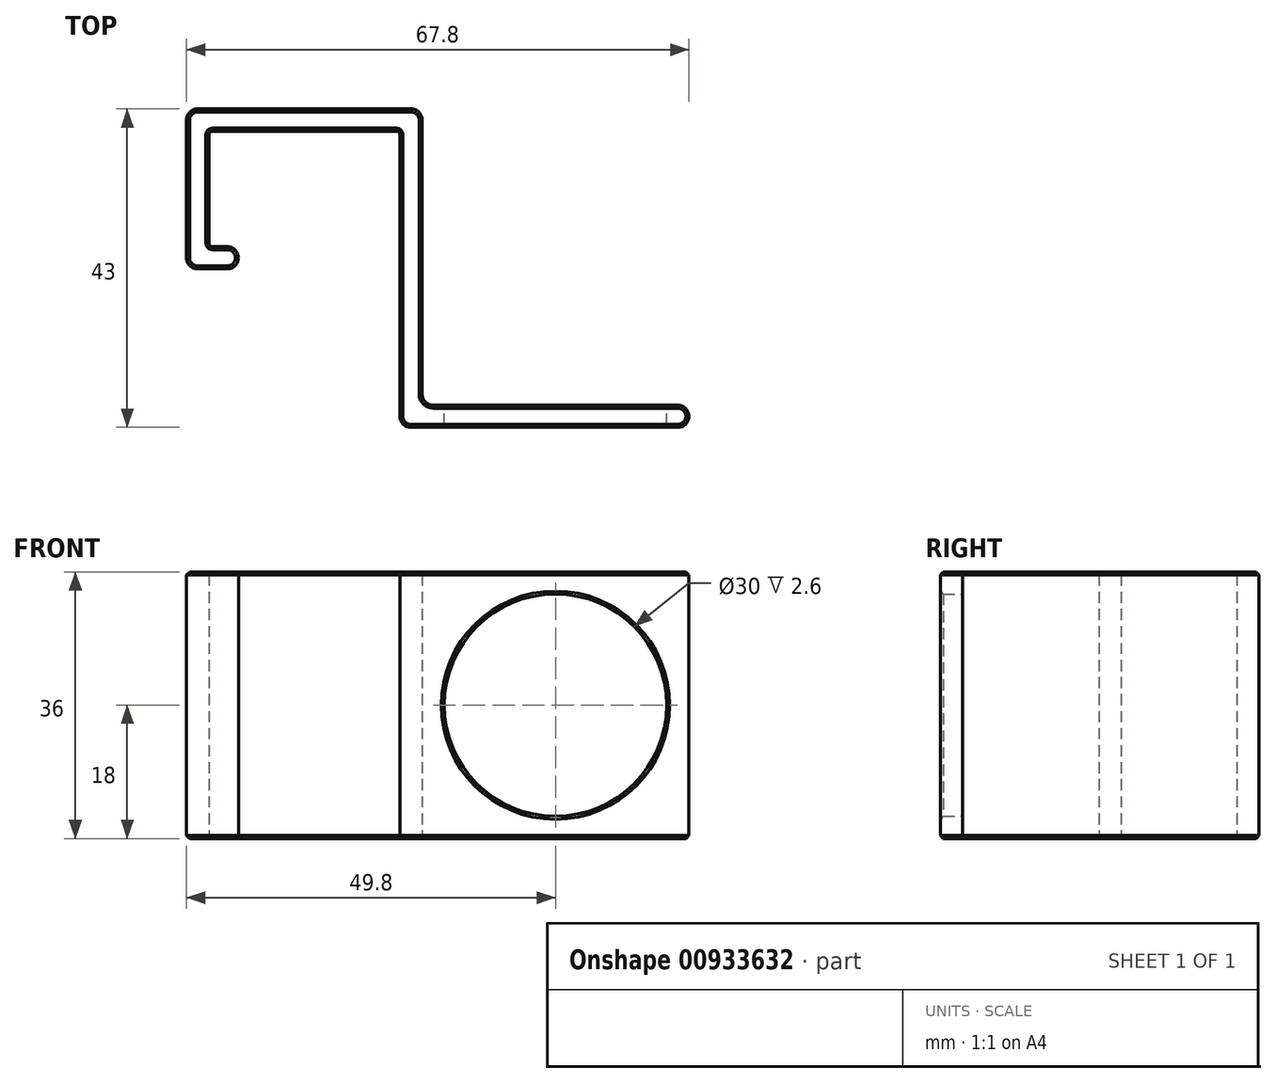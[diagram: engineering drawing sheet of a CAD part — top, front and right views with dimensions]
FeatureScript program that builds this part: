
annotation { "Feature Type Name" : "Feature", "Feature Type Description" : "" }
export const myFeature = defineFeature(function(context is Context, id is Id, definition is map)
    precondition{}
    {
        {
            var Q0;
            Q0=qCreatedBy(makeId("Top.planeOp"),FACE);
            var sketch = newSketch(context, id + "F0", { "sketchPlane" : qUnion([Q0])});
            skLineSegment(sketch, "E0", {"start": v(0, 0) * mm, "end": v(0, 18.6) * mm});
            skLineSegment(sketch, "E1", {"start": v(0, 18.6) * mm, "end": v(25.8, 18.6) * mm});
            skLineSegment(sketch, "E2", {"start": v(25.8, 18.6) * mm, "end": v(25.8, -21.4) * mm});
            skLineSegment(sketch, "E3", {"start": v(25.8, -21.4) * mm, "end": v(64.8, -21.4) * mm});
            skLineSegment(sketch, "E4.1", {"start": v(-3, 0) * mm, "end": v(-3, 21.6) * mm});
            skLineSegment(sketch, "E4.2", {"start": v(-3, 21.6) * mm, "end": v(28.8, 21.6) * mm});
            skLineSegment(sketch, "E4.3", {"start": v(28.8, 21.6) * mm, "end": v(28.8, -18.4) * mm});
            skLineSegment(sketch, "E4.4", {"start": v(28.8, -18.4) * mm, "end": v(64.8, -18.4) * mm});
            skLineSegment(sketch, "E5", {"start": v(0, 0) * mm, "end": v(-3, 0) * mm});
            skPoint(sketch, "E6", {"position": v(0, 3) * mm});
            skLineSegment(sketch, "E7", {"start": v(0, 3) * mm, "end": v(4, 3) * mm});
            skLineSegment(sketch, "E8", {"start": v(4, 3) * mm, "end": v(4, 0) * mm});
            skLineSegment(sketch, "E9", {"start": v(4, 0) * mm, "end": v(0, 0) * mm});
            skLineSegment(sketch, "E10", {"start": v(64.8, -18.4) * mm, "end": v(64.8, -21.4) * mm});
            skSolve(sketch);
        }
        {
            var Q0;
            {var subQ4=sQuery(id+"F0.wireOp",EDGE,"E1");Q0=makeQuery(id+"F0.imprint","IMPRINT",FACE,{"disambiguationData":[TD([[makeQuery(id+"F0.imprint","IMPRINT",EDGE,{"derivedFrom":subQ4}),1.0]])]});}
            var Q1;
            {var subQ2=sQuery(id+"F0.wireOp",EDGE,"E7");Q1=makeQuery(id+"F0.imprint","IMPRINT",FACE,{"disambiguationData":[TD([[makeQuery(id+"F0.imprint","IMPRINT",EDGE,{"derivedFrom":subQ2}),-1.0]])]});}
            extrude(context, id + "F1", {"entities" : qUnion([Q0, Q1]), "depth" : 36 * mm, "offsetDistance" : 25 * mm});
        }
        {
            var Q0;
            Q0=makeQuery(id+"F1.opExtrude","SWEPT_FACE",FACE,{"disambiguationData":[OSD([sQuery(id+"F0.wireOp",EDGE,"E4.4")])]});
            var sketch = newSketch(context, id + "F2", { "sketchPlane" : qUnion([Q0])});
            skPoint(sketch, "E11.0", {"position": v(-46.8, 0) * mm});
            skPoint(sketch, "E12.0", {"position": v(-28.8, 18) * mm});
            skCircle(sketch, "E13", {"center": v(-46.8, 18) * mm, "radius": 15 * mm});
            skSolve(sketch);
        }
        {
            var Q0;
            Q0=makeQuery(id+"F2.imprint","IMPRINT",FACE,{"disambiguationData":[TD([[makeQuery(id+"F2.imprint","IMPRINT",EDGE,{"derivedFrom":sQuery(id+"F2.wireOp",EDGE,"E13")}),1.0]])]});
            extrude(context, id + "F3", {"entities" : qUnion([Q0]), "operationType" : NewBodyOperationType.REMOVE, "oppositeDirection" : true, "depth" : 25 * mm, "offsetDistance" : 25 * mm});
        }
        {
            var Q0;
            Q0=makeQuery(id+"F1.opExtrude","SWEPT_EDGE",EDGE,{"disambiguationData":[OSD([sQuery(id+"F0.wireOp",EDGE,"E4.1"),sQuery(id+"F0.wireOp",EDGE,"E5")])]});
            var Q1;
            Q1=makeQuery(id+"F1.opExtrude","SWEPT_EDGE",EDGE,{"disambiguationData":[OSD([sQuery(id+"F0.wireOp",EDGE,"E4.1"),sQuery(id+"F0.wireOp",EDGE,"E4.2")])]});
            var Q2;
            Q2=makeQuery(id+"F1.opExtrude","SWEPT_EDGE",EDGE,{"disambiguationData":[OSD([sQuery(id+"F0.wireOp",EDGE,"E4.2"),sQuery(id+"F0.wireOp",EDGE,"E4.3")])]});
            var Q3;
            Q3=makeQuery(id+"F1.opExtrude","SWEPT_EDGE",EDGE,{"disambiguationData":[OSD([sQuery(id+"F0.wireOp",EDGE,"E4.3"),sQuery(id+"F0.wireOp",EDGE,"E4.4")])]});
            var Q4;
            Q4=makeQuery(id+"F1.opExtrude","SWEPT_EDGE",EDGE,{"disambiguationData":[OSD([sQuery(id+"F0.wireOp",EDGE,"E4.0"),sQuery(id+"F0.wireOp",EDGE,"E4.4")])]});
            var Q5;
            Q5=makeQuery(id+"F1.opExtrude","SWEPT_EDGE",EDGE,{"disambiguationData":[OSD([sQuery(id+"F0.wireOp",EDGE,"E4.0"),sQuery(id+"F0.wireOp",EDGE,"aEDjAN8Z-vlYd-PfeB-CgkG-z7zWKWA2CgOz")])]});
            var Q6;
            Q6=makeQuery(id+"F1.opExtrude","SWEPT_EDGE",EDGE,{"disambiguationData":[OSD([sQuery(id+"F0.wireOp",EDGE,"9RLHLQtQ-NXMR-4HYP-DCTX-MHSKpvzwpqg6"),sQuery(id+"F0.wireOp",EDGE,"aEDjAN8Z-vlYd-PfeB-CgkG-z7zWKWA2CgOz")])]});
            var Q7;
            Q7=makeQuery(id+"F1.opExtrude","SWEPT_EDGE",EDGE,{"disambiguationData":[OSD([sQuery(id+"F0.wireOp",EDGE,"E3"),sQuery(id+"F0.wireOp",EDGE,"9RLHLQtQ-NXMR-4HYP-DCTX-MHSKpvzwpqg6")])]});
            var Q8;
            Q8=makeQuery(id+"F1.opExtrude","SWEPT_EDGE",EDGE,{"disambiguationData":[OSD([sQuery(id+"F0.wireOp",EDGE,"E2"),sQuery(id+"F0.wireOp",EDGE,"E3")])]});
            var Q9;
            Q9=makeQuery(id+"F1.opExtrude","SWEPT_EDGE",EDGE,{"disambiguationData":[OSD([sQuery(id+"F0.wireOp",EDGE,"E7"),sQuery(id+"F0.wireOp",EDGE,"E8")])]});
            var Q10;
            Q10=makeQuery(id+"F1.opExtrude","SWEPT_EDGE",EDGE,{"disambiguationData":[OSD([sQuery(id+"F0.wireOp",EDGE,"E8"),sQuery(id+"F0.wireOp",EDGE,"E9")])]});
            fillet(context, id + "F4", {"entities" : qUnion([Q0, Q1, Q2, Q3, Q4, Q5, Q6, Q7, Q8, Q9, Q10]), "radius" : 1.5 * mm, "tangentPropagation" : true, "allowEdgeOverflow" : false});
        }
        {
            var Q0;
            Q0=makeQuery(id+"F1.opExtrude","SWEPT_EDGE",EDGE,{"disambiguationData":[OSD([sQuery(id+"F0.wireOp",EDGE,"E0"),sQuery(id+"F0.wireOp",EDGE,"E1")])]});
            var Q1;
            Q1=makeQuery(id+"F1.opExtrude","SWEPT_EDGE",EDGE,{"disambiguationData":[OSD([sQuery(id+"F0.wireOp",EDGE,"E1"),sQuery(id+"F0.wireOp",EDGE,"E2")])]});
            var Q2;
            Q2=makeQuery(id+"F1.opExtrude","SWEPT_EDGE",EDGE,{"disambiguationData":[OSD([sQuery(id+"F0.wireOp",EDGE,"E0"),sQuery(id+"F0.wireOp",EDGE,"E7")])]});
            fillet(context, id + "F5", {"entities" : qUnion([Q0, Q1, Q2]), "radius" : 0.5 * mm, "tangentPropagation" : true, "allowEdgeOverflow" : false});
        }
        {
            var Q0;
            Q0=makeQuery(id+"F1.opExtrude","CAP_FACE",FACE,{"disambiguationData":[OSD([sQuery(id+"F0.wireOp",EDGE,"E0"),sQuery(id+"F0.wireOp",EDGE,"E1"),sQuery(id+"F0.wireOp",EDGE,"E2"),sQuery(id+"F0.wireOp",EDGE,"E3"),sQuery(id+"F0.wireOp",EDGE,"9RLHLQtQ-NXMR-4HYP-DCTX-MHSKpvzwpqg6"),sQuery(id+"F0.wireOp",EDGE,"E4.0"),sQuery(id+"F0.wireOp",EDGE,"E4.1"),sQuery(id+"F0.wireOp",EDGE,"E4.2"),sQuery(id+"F0.wireOp",EDGE,"E4.3"),sQuery(id+"F0.wireOp",EDGE,"E4.4"),sQuery(id+"F0.wireOp",EDGE,"E5"),sQuery(id+"F0.wireOp",EDGE,"aEDjAN8Z-vlYd-PfeB-CgkG-z7zWKWA2CgOz")])],"isStart":false});
            var Q1;
            Q1=makeQuery(id+"F1.opExtrude","CAP_FACE",FACE,{"disambiguationData":[OSD([sQuery(id+"F0.wireOp",EDGE,"E0"),sQuery(id+"F0.wireOp",EDGE,"E1"),sQuery(id+"F0.wireOp",EDGE,"E2"),sQuery(id+"F0.wireOp",EDGE,"E3"),sQuery(id+"F0.wireOp",EDGE,"9RLHLQtQ-NXMR-4HYP-DCTX-MHSKpvzwpqg6"),sQuery(id+"F0.wireOp",EDGE,"E4.0"),sQuery(id+"F0.wireOp",EDGE,"E4.1"),sQuery(id+"F0.wireOp",EDGE,"E4.2"),sQuery(id+"F0.wireOp",EDGE,"E4.3"),sQuery(id+"F0.wireOp",EDGE,"E4.4"),sQuery(id+"F0.wireOp",EDGE,"E5"),sQuery(id+"F0.wireOp",EDGE,"aEDjAN8Z-vlYd-PfeB-CgkG-z7zWKWA2CgOz")])],"isStart":true});
            var Q2;
            Q2=makeQuery(id+"F3.boolean.opBoolean","COPY",EDGE,{"derivedFrom":makeQuery(id+"F3.opExtrude","CAP_EDGE",EDGE,{"disambiguationData":[OSD([sQuery(id+"F2.wireOp",EDGE,"E13")])],"isStart":true})});
            var Q3;
            Q3=makeQuery(id+"F3.boolean.opBoolean","INTERSECT",EDGE,{"derivedFrom":[makeQuery(id+"F1.opExtrude","SWEPT_FACE",FACE,{"disambiguationData":[OSD([sQuery(id+"F0.wireOp",EDGE,"E3")])]}),makeQuery(id+"F3.opExtrude","SWEPT_FACE",FACE,{"disambiguationData":[OSD([sQuery(id+"F2.wireOp",EDGE,"E13")])]})]});
            chamfer(context, id + "F6", {"entities" : qUnion([Q0, Q1, Q2, Q3]), "width" : 0.4 * mm, "tangentPropagation" : true});
        }
    });
